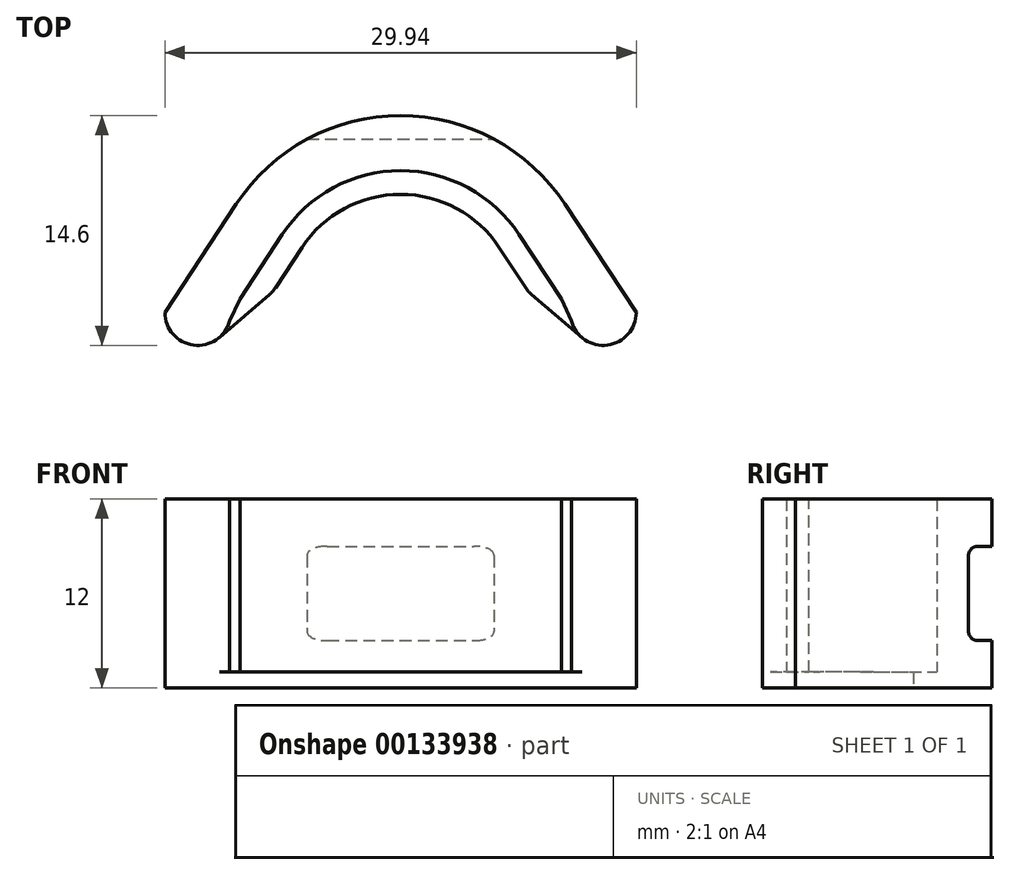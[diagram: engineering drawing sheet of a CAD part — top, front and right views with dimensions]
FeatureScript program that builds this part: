
annotation { "Feature Type Name" : "Feature", "Feature Type Description" : "" }
export const myFeature = defineFeature(function(context is Context, id is Id, definition is map)
    precondition{}
    {
        {
            var Q0;
            Q0=qCreatedBy(makeId("Top.planeOp"),FACE);
            var sketch = newSketch(context, id + "F0", { "sketchPlane" : qUnion([Q0])});
            skLineSegment(sketch, "E0", {"start": v(-7.52, 24.95) * mm, "end": v(-7.52, 24.95) * mm});
            skLineSegment(sketch, "E1", {"start": v(7.52, 24.95) * mm, "end": v(12.1, 17.98) * mm});
            skLineSegment(sketch, "E2", {"start": v(-7.52, 24.95) * mm, "end": v(-12.1, 17.97) * mm});
            skArc(sketch, "E3", {"start": v(7.52, 24.95) * mm, "mid": v(0, 29) * mm, "end": v(-7.52, 24.95) * mm});
            skArc(sketch, "E4", {"start": v(-7.52, 24.95) * mm, "mid": v(0, 11) * mm, "end": v(7.52, 24.95) * mm, "construction": true});
            skArc(sketch, "E5", {"start": v(-16.7, 11) * mm, "mid": v(0, -20) * mm, "end": v(16.7, 11) * mm, "construction": true});
            skArc(sketch, "E6", {"start": v(16.7, 11) * mm, "mid": v(0, 20) * mm, "end": v(-16.7, 11) * mm, "construction": true});
            skLineSegment(sketch, "E7", {"start": v(0, 29) * mm, "end": v(0, 20) * mm, "construction": true});
            skLineSegment(sketch, "E8", {"start": v(-14.97, 20) * mm, "end": v(-10.78, 20) * mm});
            skPoint(sketch, "E8.startSnap0", {"position": v(-12.1, 17.97) * mm});
            skPoint(sketch, "E9", {"position": v(12.1, 17.98) * mm});
            skLineSegment(sketch, "E10", {"start": v(-12.1, 17.97) * mm, "end": v(-16.7, 11) * mm, "construction": true});
            skLineSegment(sketch, "E11", {"start": v(12.1, 17.98) * mm, "end": v(16.7, 11) * mm, "construction": true});
            skLineSegment(sketch, "E12.0", {"start": v(-10.44, 26.87) * mm, "end": v(-14.97, 20) * mm});
            skArc(sketch, "E12.1", {"start": v(10.44, 26.87) * mm, "mid": v(0, 32.5) * mm, "end": v(-10.44, 26.87) * mm});
            skLineSegment(sketch, "E12.2", {"start": v(10.44, 26.88) * mm, "end": v(14.97, 20) * mm});
            skLineSegment(sketch, "E13", {"start": v(-10.78, 20) * mm, "end": v(10.78, 20) * mm, "construction": true});
            skLineSegment(sketch, "E14", {"start": v(10.78, 20) * mm, "end": v(14.97, 20) * mm});
            skArc(sketch, "E15", {"start": v(-14.97, 20) * mm, "mid": v(-11.12, 18.85) * mm, "end": v(-13.7, 21.92) * mm});
            skArc(sketch, "E16", {"start": v(10.78, 20) * mm, "mid": v(12.87, 17.9) * mm, "end": v(14.97, 20) * mm});
            skPoint(sketch, "E17", {"position": v(-7.52, 24.95) * mm});
            skPoint(sketch, "E18", {"position": v(7.52, 24.95) * mm});
            skSolve(sketch);
        }
        {
            var Q0;
            Q0 = qSketchRegion(id + "F0", true);
            extrude(context, id + "F1", {"entities" : qUnion([Q0]), "depth" : 12 * mm});
        }
        {
            var Q0;
            Q0=qCreatedBy(makeId("Right.planeOp"),FACE);
            var sketch = newSketch(context, id + "F2", { "sketchPlane" : qUnion([Q0])});
            skLineSegment(sketch, "E19", {"start": v(32.5, 9) * mm, "end": v(32.5, 3) * mm});
            skLineSegment(sketch, "E20.0", {"start": v(31, 9) * mm, "end": v(31, 3) * mm});
            skLineSegment(sketch, "E21.0", {"start": v(31, 9) * mm, "end": v(32.5, 9) * mm});
            skLineSegment(sketch, "E22.0", {"start": v(31, 3) * mm, "end": v(32.5, 3) * mm});
            skLineSegment(sketch, "E23", {"start": v(32.5, 12) * mm, "end": v(32.5, 9) * mm, "construction": true});
            skLineSegment(sketch, "E24.0", {"start": v(26.87, 0) * mm, "end": v(32.5, 0) * mm, "construction": true});
            skLineSegment(sketch, "E25", {"start": v(32.5, 3) * mm, "end": v(32.5, 0) * mm, "construction": true});
            skLineSegment(sketch, "E26", {"start": v(32.5, 9) * mm, "end": v(32.5, 3) * mm, "construction": true});
            skSolve(sketch);
        }
        {
            var Q0;
            Q0 = qSketchRegion(id + "F2", true);
            extrude(context, id + "F3", {"entities" : qUnion([Q0]), "operationType" : NewBodyOperationType.REMOVE, "endBound" : BoundingType.SYMMETRIC, "oppositeDirection" : true, "depth" : 25 * mm});
        }
        {
            var Q0;
            Q0=makeQuery(id+"F3.boolean.opBoolean","COPY",EDGE,{"derivedFrom":makeQuery(id+"F3.opExtrude","SWEPT_EDGE",EDGE,{"disambiguationData":[OSD([sQuery(id+"F2.wireOp",EDGE,"E20.0"),sQuery(id+"F2.wireOp",EDGE,"E21.0")])]})});
            var Q1;
            Q1=makeQuery(id+"F3.boolean.opBoolean","COPY",EDGE,{"derivedFrom":makeQuery(id+"F3.opExtrude","SWEPT_EDGE",EDGE,{"disambiguationData":[OSD([sQuery(id+"F2.wireOp",EDGE,"E20.0"),sQuery(id+"F2.wireOp",EDGE,"E22.0")])]})});
            fillet(context, id + "F4", {"entities" : qUnion([Q0, Q1]), "radius" : .6 * mm, "tangentPropagation" : true, "allowEdgeOverflow" : false});
        }
        {
            var Q0;
            Q0=makeQuery(id+"F1.opExtrude","SWEPT_EDGE",EDGE,{"disambiguationData":[OSD([sQuery(id+"F0.wireOp",EDGE,"E1"),sQuery(id+"F0.wireOp",EDGE,"E14"),sQuery(id+"F0.wireOp",EDGE,"E16")])]});
            var Q1;
            Q1=makeQuery(id+"F1.opExtrude","SWEPT_EDGE",EDGE,{"disambiguationData":[OSD([sQuery(id+"F0.wireOp",EDGE,"E2"),sQuery(id+"F0.wireOp",EDGE,"E8"),sQuery(id+"F0.wireOp",EDGE,"E15")])]});
            chamfer(context, id + "F5", {"entities" : qUnion([Q0, Q1]), "width" : 5 * mm, "tangentPropagation" : true});
        }
        {
            var Q0;
            Q0=makeQuery(id+"F1.opExtrude","CAP_FACE",FACE,{"disambiguationData":[OSD([sQuery(id+"F0.wireOp",EDGE,"E1"),sQuery(id+"F0.wireOp",EDGE,"E2"),sQuery(id+"F0.wireOp",EDGE,"E3"),sQuery(id+"F0.wireOp",EDGE,"E12.0"),sQuery(id+"F0.wireOp",EDGE,"E12.1"),sQuery(id+"F0.wireOp",EDGE,"E12.2"),sQuery(id+"F0.wireOp",EDGE,"E15"),sQuery(id+"F0.wireOp",EDGE,"E16")])],"isStart":true});
            var sketch = newSketch(context, id + "F6", { "sketchPlane" : qUnion([Q0])});
            skArc(sketch, "E27.0", {"start": v(7.52, -24.95) * mm, "mid": v(0, -29) * mm, "end": v(-7.52, -24.95) * mm});
            skLineSegment(sketch, "E28.0", {"start": v(7.52, -24.95) * mm, "end": v(9.44, -22.03) * mm});
            skLineSegment(sketch, "E29.0", {"start": v(-6.26, -24.12) * mm, "end": v(-11.7, -15.88) * mm});
            skArc(sketch, "E29.1", {"start": v(6.26, -24.12) * mm, "mid": v(0, -27.5) * mm, "end": v(-6.26, -24.12) * mm});
            skLineSegment(sketch, "E29.2", {"start": v(6.26, -24.13) * mm, "end": v(7.95, -21.56) * mm});
            skLineSegment(sketch, "E30", {"start": v(8.1, -21.33) * mm, "end": v(9.44, -22.03) * mm, "construction": true});
            skLineSegment(sketch, "E31", {"start": v(8.32, -21.14) * mm, "end": v(11.5, -18.4) * mm});
            skPoint(sketch, "E32.visualSharp", {"position": v(8.1, -21.33) * mm});
            skArc(sketch, "E32.filletArc", {"start": v(8.32, -21.14) * mm, "mid": v(8.12, -21.34) * mm, "end": v(7.95, -21.56) * mm});
            skLineSegment(sketch, "E33", {"start": v(0, 0) * mm, "end": v(0, -31.42) * mm, "construction": true});
            skLineSegment(sketch, "E34.MirrorCS", {"start": v(-8.32, -21.14) * mm, "end": v(-11.5, -18.4) * mm});
            skArc(sketch, "E35.MirrorCS", {"start": v(-8.32, -21.14) * mm, "mid": v(-8.12, -21.34) * mm, "end": v(-7.95, -21.56) * mm});
            skLineSegment(sketch, "E36.MirrorCS", {"start": v(-6.26, -24.13) * mm, "end": v(-7.95, -21.56) * mm});
            skSolve(sketch);
        }
        {
            var Q0;
            Q0=makeQuery(id+"F6.imprint","IMPRINT",FACE,{"disambiguationData":[TD([[makeQuery(id+"F6.imprint","IMPRINT",EDGE,{"derivedFrom":sQuery(id+"F6.wireOp",EDGE,"E27.0")}),-1.0]])]});
            extrude(context, id + "F7", {"entities" : qUnion([Q0]), "operationType" : NewBodyOperationType.ADD, "oppositeDirection" : true, "depth" : 1 * mm});
        }
    });
